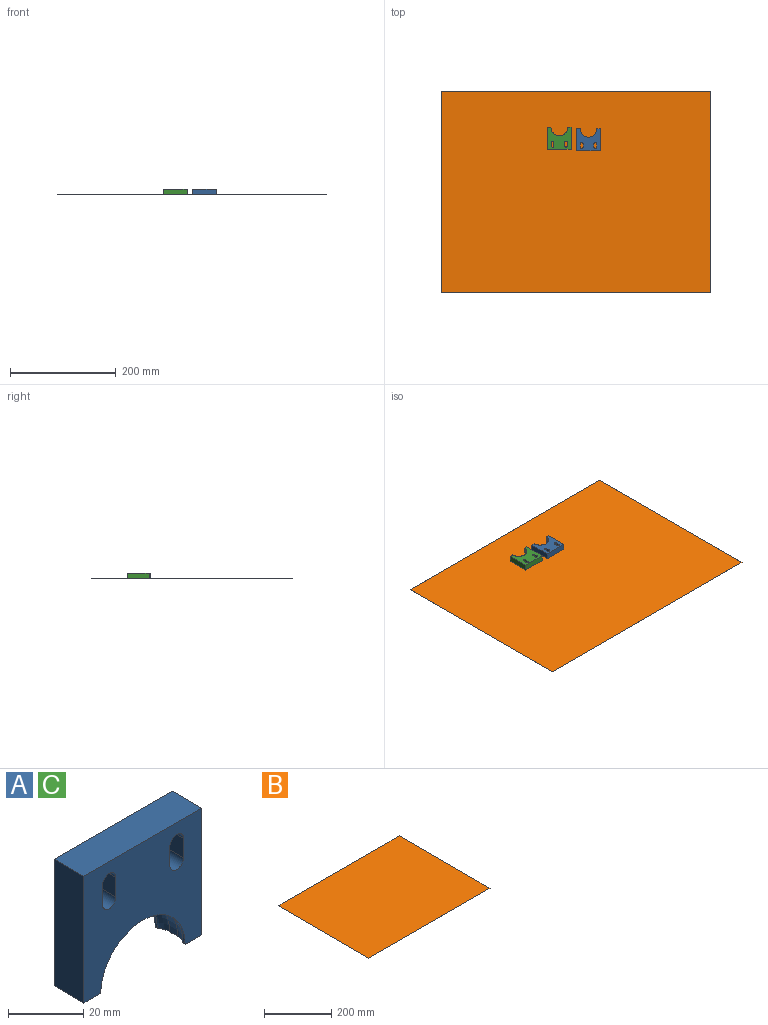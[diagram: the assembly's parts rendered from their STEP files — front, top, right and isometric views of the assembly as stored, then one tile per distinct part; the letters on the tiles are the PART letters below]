
ASSEMBLY  parts=3 mates=2
PART A: 20 faces, bbox 44.5x11.3x41.3 mm
  f0: plane 44.45x41.28mm, normal (0,-1,0), area 1333mm2, adj f2,f3,f4,f5,f6,f8,f12,f13
  f1: plane 44.45x41.28mm, normal (0,1,0), area 1333mm2, adj f2,f4,f5,f6,f7,f8,f12,f13
  f2: plane 11.25x6.35mm, normal (0,0,-1), area 61.8mm2, adj f0,f1,f3,f6,f7,f9,f10,f11
  f3: cylinder r=15.88mm len=31.75mm, axis (0,1,0), area 38mm2, adj f0,f2,f4,f11
  f4: plane 11.25x6.35mm, normal (0,0,-1), area 61.8mm2, adj f0,f1,f3,f7,f8,f9,f10,f11
  f5: plane 44.45x11.25mm, normal (0,0,1), area 500.2mm2, adj f0,f1,f6,f8
  f6: plane 41.28x11.25mm, normal (-1,0,0), area 464.4mm2, adj f0,f1,f2,f5
  f7: cylinder r=15.88mm len=31.75mm, axis (0,1,0), area 38mm2, adj f1,f2,f4,f10
  f8: plane 41.28x11.25mm, normal (1,0,0), area 464.4mm2, adj f0,f1,f4,f5
  f9: cylinder r=17.14mm len=34.29mm, axis (0,1,0), area 162mm2, adj f2,f4,f10,f11
  f10: torus R=12.06mm, axis (0,1,0), area 192.8mm2, adj f2,f4,f7,f9
  f11: torus R=12.06mm, axis (0,-1,0), area 192.8mm2, adj f2,f3,f4,f9
  f12: cylinder r=2.55mm len=11.25mm, axis (0,-1,0), area 90.2mm2, adj f0,f1,f13,f15
  f13: plane 11.25x6.35mm, normal (1,0,0), area 71.5mm2, adj f0,f1,f12,f14
  f14: cylinder r=2.55mm len=11.25mm, axis (0,-1,0), area 90.2mm2, adj f0,f1,f13,f15
  f15: plane 11.25x6.35mm, normal (-1,0,0), area 71.5mm2, adj f0,f1,f12,f14
  f16: cylinder r=2.55mm len=11.25mm, axis (0,-1,0), area 90.2mm2, adj f0,f1,f17,f19
  f17: plane 11.25x6.35mm, normal (1,0,0), area 71.5mm2, adj f0,f1,f16,f18
  f18: cylinder r=2.55mm len=11.25mm, axis (0,-1,0), area 90.2mm2, adj f0,f1,f17,f19
  f19: plane 11.25x6.35mm, normal (-1,0,0), area 71.5mm2, adj f0,f1,f16,f18
PART B: 6 faces, bbox 508x381x0 mm
  f0: plane 508x0.03mm, normal (0,1,0), area 12.9mm2, adj f1,f3,f4,f5
  f1: plane 381x0.03mm, normal (-1,0,0), area 9.7mm2, adj f0,f2,f4,f5
  f2: plane 508x0.03mm, normal (0,-1,0), area 12.9mm2, adj f1,f3,f4,f5
  f3: plane 381x0.03mm, normal (1,0,0), area 9.7mm2, adj f0,f2,f4,f5
  f4: plane 508x381mm, normal (0,0,1), area 193548mm2, adj f0,f1,f2,f3
  f5: plane 508x381mm, normal (0,0,-1), area 193548mm2, adj f0,f1,f2,f3
PART C: same geometry as A
PLACE A rot(axis=(1,0,0),90deg) t=(23.6,56.67,5.65)mm
PLACE B at identity fixed
PLACE C rot(axis=(1,0,0),90deg) t=(-31.57,59.34,5.65)mm
MATE planar A.f0 <-> B.f4  axis (0,0,-1) through (23.6,32.78,0.03)mm
MATE planar B.f4 <-> C.f0  axis (0,0,1) through (0,-63.12,0.03)mm
